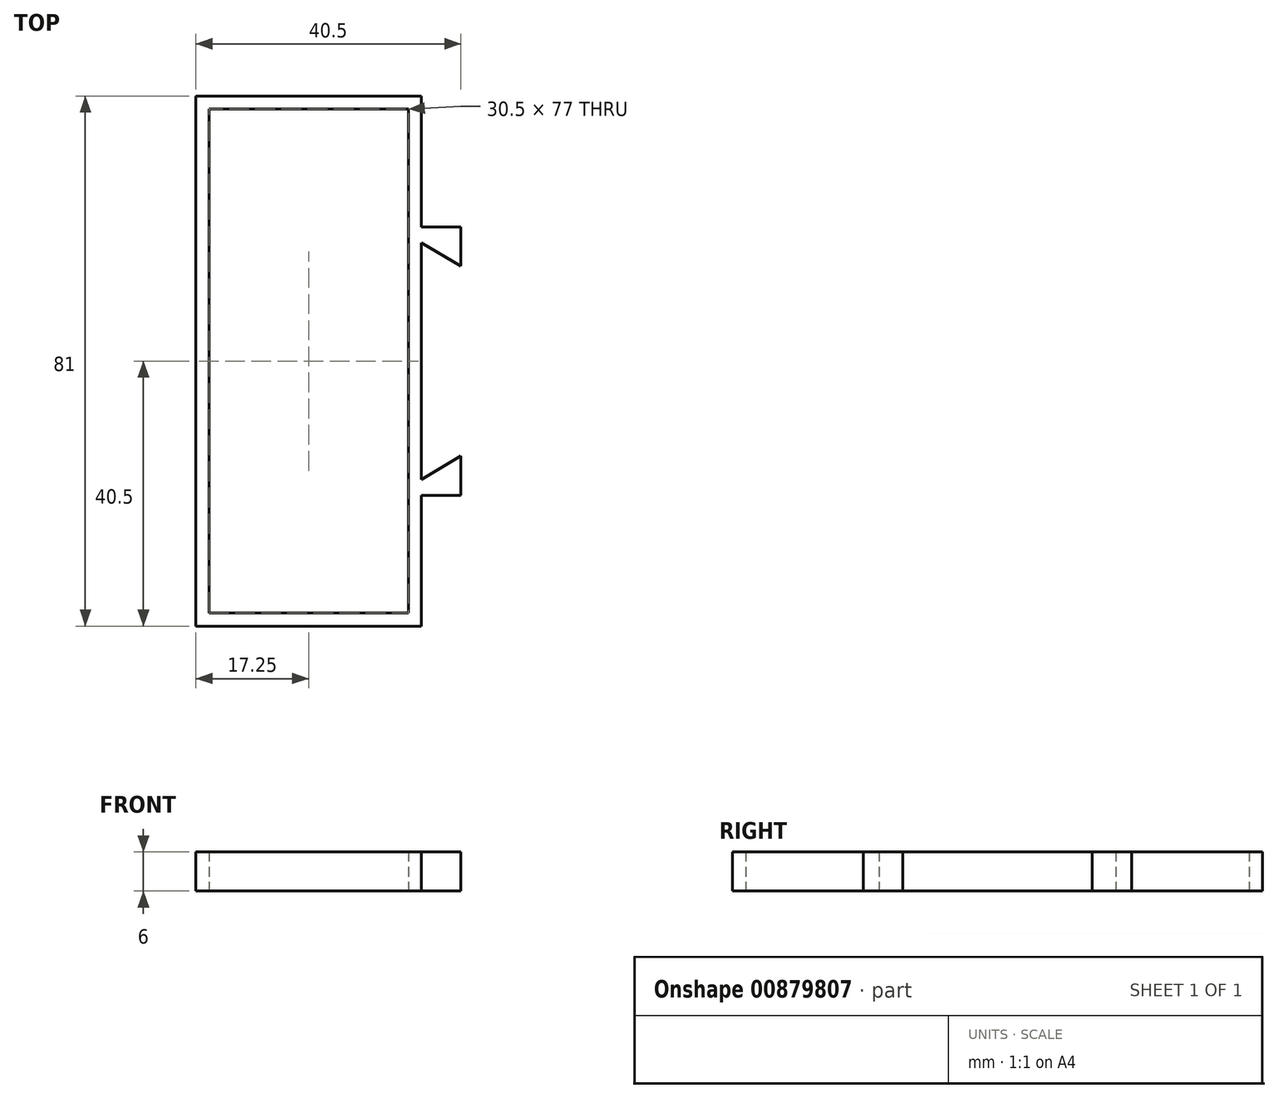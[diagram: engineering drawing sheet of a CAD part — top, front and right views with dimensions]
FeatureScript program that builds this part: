
annotation { "Feature Type Name" : "Feature", "Feature Type Description" : "" }
export const myFeature = defineFeature(function(context is Context, id is Id, definition is map)
    precondition{}
    {
        {
            var Q0;
            Q0=qCreatedBy(makeId("Top.planeOp"),FACE);
            var sketch = newSketch(context, id + "F0", { "sketchPlane" : qUnion([Q0])});
            skLineSegment(sketch, "E0.bottom", {"start": v(15.25, -38.5) * mm, "end": v(-15.25, -38.5) * mm});
            skLineSegment(sketch, "E0.top", {"start": v(15.25, 38.5) * mm, "end": v(-15.25, 38.5) * mm});
            skLineSegment(sketch, "E0.left", {"start": v(15.25, -38.5) * mm, "end": v(15.25, 38.5) * mm});
            skLineSegment(sketch, "E0.right", {"start": v(-15.25, -38.5) * mm, "end": v(-15.25, 38.5) * mm});
            skPoint(sketch, "E0.middle", {"position": v(0, 0) * mm});
            skLineSegment(sketch, "E1.0", {"start": v(17.25, -40.5) * mm, "end": v(17.25, -18.1) * mm});
            skLineSegment(sketch, "E1.1", {"start": v(17.25, -40.5) * mm, "end": v(-17.25, -40.5) * mm});
            skLineSegment(sketch, "E1.2", {"start": v(-17.25, -40.5) * mm, "end": v(-17.25, 40.5) * mm});
            skLineSegment(sketch, "E1.3", {"start": v(17.25, 40.5) * mm, "end": v(-17.25, 40.5) * mm});
            skLineSegment(sketch, "E2.top", {"start": v(17.25, -20.5) * mm, "end": v(23.25, -20.5) * mm});
            skLineSegment(sketch, "E2.left", {"start": v(17.25, -11.06) * mm, "end": v(17.25, -20.5) * mm});
            skLineSegment(sketch, "E2.right", {"start": v(23.25, -14.5) * mm, "end": v(23.25, -20.5) * mm});
            skLineSegment(sketch, "E3", {"start": v(23.25, -14.5) * mm, "end": v(17.25, -18.1) * mm});
            skLineSegment(sketch, "E4.trimOffspring", {"start": v(17.25, -11.06) * mm, "end": v(17.25, 40.5) * mm});
            skLineSegment(sketch, "E5.MirrorCS", {"start": v(17.25, 20.5) * mm, "end": v(23.25, 20.5) * mm});
            skLineSegment(sketch, "E6.MirrorCS", {"start": v(23.25, 14.5) * mm, "end": v(17.25, 18.1) * mm});
            skLineSegment(sketch, "E7.MirrorCS", {"start": v(17.25, 40.5) * mm, "end": v(17.25, 18.1) * mm});
            skLineSegment(sketch, "E8.MirrorCS", {"start": v(17.25, 11.06) * mm, "end": v(17.25, 20.5) * mm});
            skLineSegment(sketch, "E9.MirrorCS", {"start": v(23.25, 14.5) * mm, "end": v(23.25, 20.5) * mm});
            skSolve(sketch);
        }
        {
            var Q0;
            {var subQ0=sQuery(id+"F0.wireOp",EDGE,"E2.top");Q0=makeQuery(id+"F0.imprint","IMPRINT",FACE,{"disambiguationData":[TD([[makeQuery(id+"F0.imprint","IMPRINT",EDGE,{"derivedFrom":subQ0}),1.0]])]});}
            var Q1;
            Q1=makeQuery(id+"F0.imprint","IMPRINT",FACE,{"disambiguationData":[TD([[makeQuery(id+"F0.imprint","IMPRINT",EDGE,{"derivedFrom":sQuery(id+"F0.wireOp",EDGE,"E0.bottom")}),1.0]])]});
            var Q2;
            {var subQ0=sQuery(id+"F0.wireOp",EDGE,"E5.MirrorCS");Q2=makeQuery(id+"F0.imprint","IMPRINT",FACE,{"disambiguationData":[TD([[makeQuery(id+"F0.imprint","IMPRINT",EDGE,{"derivedFrom":subQ0}),-1.0]])]});}
            extrude(context, id + "F1", {"entities" : qUnion([Q0, Q1, Q2]), "depth" : 6 * mm, "offsetDistance" : 25 * mm});
        }
    });
